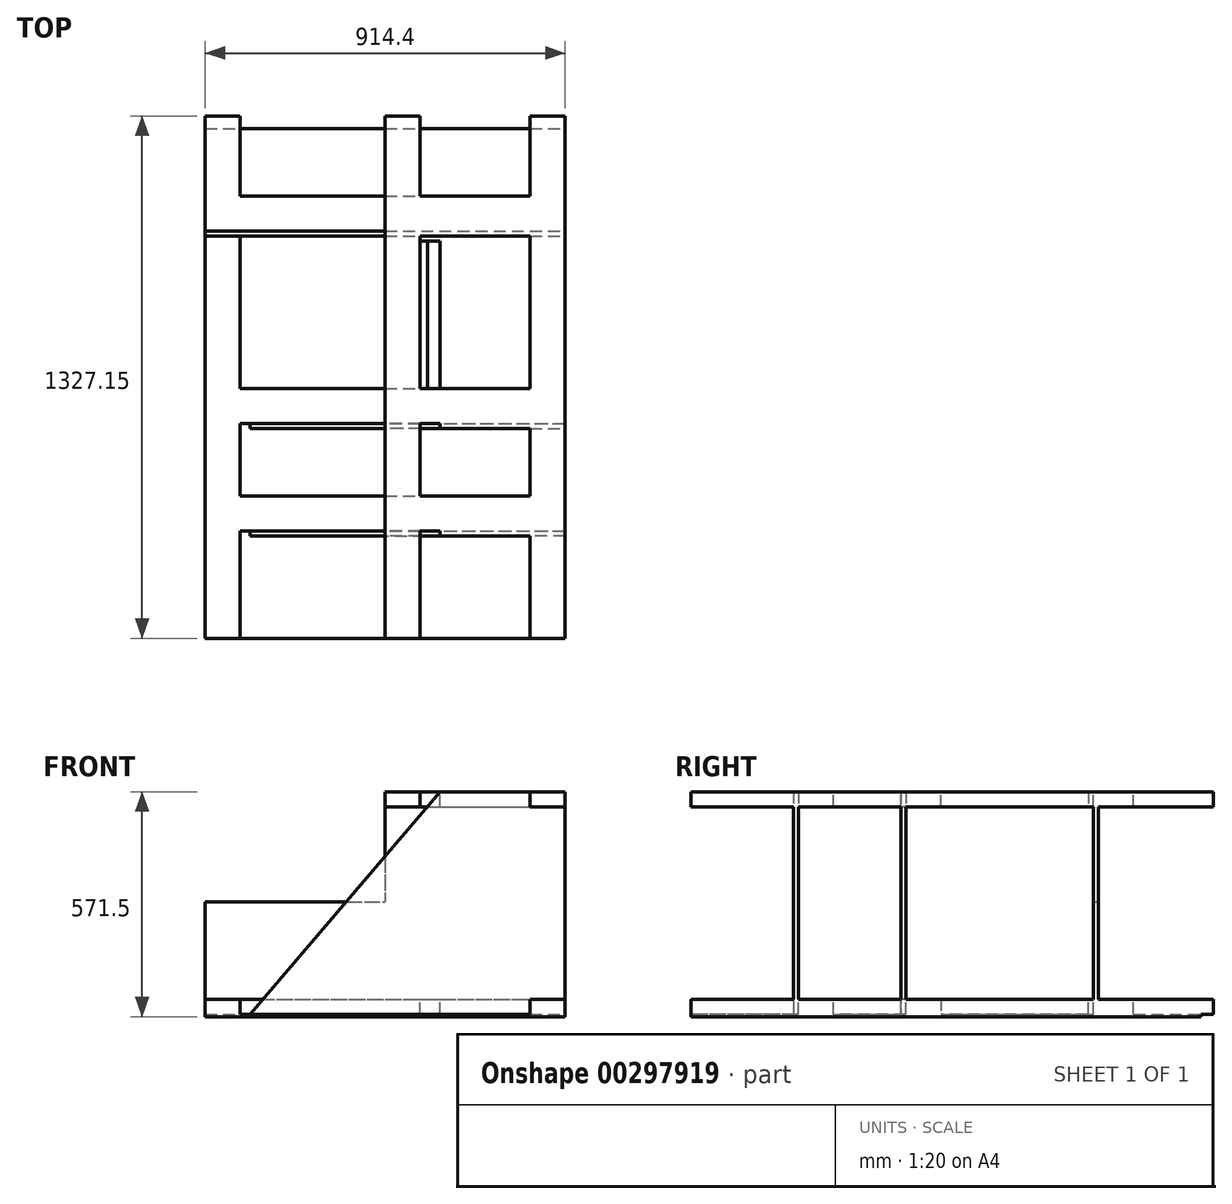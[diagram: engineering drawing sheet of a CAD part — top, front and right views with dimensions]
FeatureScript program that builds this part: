
annotation { "Feature Type Name" : "Feature", "Feature Type Description" : "" }
export const myFeature = defineFeature(function(context is Context, id is Id, definition is map)
    precondition{}
    {
        {
            var Q0;
            Q0=qCreatedBy(makeId("Front.planeOp"),FACE);
            var sketch = newSketch(context, id + "F0", { "sketchPlane" : qUnion([Q0])});
            skLineSegment(sketch, "E0.bottom", {"start": v(0, 0) * mm, "end": v(914.4, 0) * mm});
            skLineSegment(sketch, "E0.top", {"start": v(0, 565.15) * mm, "end": v(914.4, 565.15) * mm});
            skLineSegment(sketch, "E0.left", {"start": v(0, 0) * mm, "end": v(0, 565.15) * mm});
            skLineSegment(sketch, "E0.right", {"start": v(914.4, 0) * mm, "end": v(914.4, 565.15) * mm});
            skSolve(sketch);
        }
        {
            var Q0;
            Q0=makeQuery(id+"F0.imprint","IMPRINT",FACE,{"disambiguationData":[TD([[makeQuery(id+"F0.imprint","IMPRINT",EDGE,{"derivedFrom":sQuery(id+"F0.wireOp",EDGE,"E0.bottom")}),1.0]])]});
            extrude(context, id + "F1", {"entities" : qUnion([Q0]), "depth" : 1327.15 * mm});
        }
        {
            var Q0;
            Q0=makeQuery(id+"F1.opExtrude","SWEPT_FACE",FACE,{"disambiguationData":[OSD([sQuery(id+"F0.wireOp",EDGE,"E0.left")])]});
            var sketch = newSketch(context, id + "F2", { "sketchPlane" : qUnion([Q0])});
            skLineSegment(sketch, "E1.bottom", {"start": v(0, 565.15) * mm, "end": v(292.1, 565.15) * mm});
            skLineSegment(sketch, "E1.top", {"start": v(0, 285.75) * mm, "end": v(292.1, 285.75) * mm});
            skLineSegment(sketch, "E1.left", {"start": v(0, 565.15) * mm, "end": v(0, 285.75) * mm});
            skLineSegment(sketch, "E1.right", {"start": v(292.1, 565.15) * mm, "end": v(292.1, 285.75) * mm});
            skSolve(sketch);
        }
        {
            var Q0;
            Q0=makeQuery(id+"F2.imprint","IMPRINT",FACE,{"disambiguationData":[TD([[makeQuery(id+"F2.imprint","IMPRINT",EDGE,{"derivedFrom":sQuery(id+"F2.wireOp",EDGE,"E1.bottom")}),1.0]])]});
            extrude(context, id + "F3", {"entities" : qUnion([Q0]), "operationType" : NewBodyOperationType.REMOVE, "oppositeDirection" : true, "depth" : 457.2 * mm});
        }
        {
            var Q0;
            Q0=makeQuery(id+"F1.opExtrude","CAP_FACE",FACE,{"disambiguationData":[OSD([sQuery(id+"F0.wireOp",EDGE,"E0.bottom"),sQuery(id+"F0.wireOp",EDGE,"E0.top"),sQuery(id+"F0.wireOp",EDGE,"E0.left"),sQuery(id+"F0.wireOp",EDGE,"E0.right")])],"isStart":false});
            var sketch = newSketch(context, id + "F4", { "sketchPlane" : qUnion([Q0])});
            skLineSegment(sketch, "E2", {"start": v(825.5, 565.15) * mm, "end": v(825.5, 527.05) * mm});
            skLineSegment(sketch, "E3", {"start": v(825.5, 527.05) * mm, "end": v(914.4, 527.05) * mm});
            skLineSegment(sketch, "E4", {"start": v(825.5, 565.15) * mm, "end": v(546.1, 565.15) * mm});
            skLineSegment(sketch, "E5", {"start": v(914.4, 527.05) * mm, "end": v(914.4, 38.1) * mm});
            skLineSegment(sketch, "E6", {"start": v(914.4, 38.1) * mm, "end": v(825.5, 38.1) * mm});
            skLineSegment(sketch, "E7", {"start": v(825.5, 38.1) * mm, "end": v(825.5, 0) * mm});
            skLineSegment(sketch, "E8", {"start": v(825.5, 0) * mm, "end": v(88.9, 0) * mm});
            skLineSegment(sketch, "E9", {"start": v(88.9, 0) * mm, "end": v(88.9, 38.1) * mm});
            skLineSegment(sketch, "E10", {"start": v(88.9, 38.1) * mm, "end": v(0, 38.1) * mm});
            skLineSegment(sketch, "E11", {"start": v(0, 38.1) * mm, "end": v(0, 565.15) * mm});
            skLineSegment(sketch, "E12", {"start": v(546.1, 565.15) * mm, "end": v(546.1, 527.05) * mm});
            skLineSegment(sketch, "E13", {"start": v(546.1, 527.05) * mm, "end": v(457.2, 527.05) * mm});
            skLineSegment(sketch, "E14", {"start": v(457.2, 527.05) * mm, "end": v(457.2, 565.15) * mm});
            skLineSegment(sketch, "E15", {"start": v(457.2, 565.15) * mm, "end": v(0, 565.15) * mm});
            skSolve(sketch);
        }
        {
            var Q0;
            Q0=makeQuery(id+"F4.imprint","IMPRINT",FACE,{"disambiguationData":[TD([[makeQuery(id+"F4.imprint","IMPRINT",EDGE,{"derivedFrom":sQuery(id+"F4.wireOp",EDGE,"E2")}),-1.0]])]});
            extrude(context, id + "F5", {"entities" : qUnion([Q0]), "operationType" : NewBodyOperationType.REMOVE, "oppositeDirection" : true, "depth" : 260.35 * mm});
        }
        {
            var Q0;
            Q0=makeQuery(id+"F5.boolean.opBoolean","COPY",FACE,{"derivedFrom":makeQuery(id+"F5.opExtrude","CAP_FACE",FACE,{"disambiguationData":[OSD([sQuery(id+"F4.wireOp",EDGE,"E2"),sQuery(id+"F4.wireOp",EDGE,"E3"),sQuery(id+"F4.wireOp",EDGE,"E4"),sQuery(id+"F4.wireOp",EDGE,"E5"),sQuery(id+"F4.wireOp",EDGE,"E6"),sQuery(id+"F4.wireOp",EDGE,"E7"),sQuery(id+"F4.wireOp",EDGE,"E8"),sQuery(id+"F4.wireOp",EDGE,"E9"),sQuery(id+"F4.wireOp",EDGE,"E10"),sQuery(id+"F4.wireOp",EDGE,"E11"),sQuery(id+"F4.wireOp",EDGE,"E12"),sQuery(id+"F4.wireOp",EDGE,"E13"),sQuery(id+"F4.wireOp",EDGE,"E14"),sQuery(id+"F4.wireOp",EDGE,"E15")])],"isStart":false})});
            var sketch = newSketch(context, id + "F6", { "sketchPlane" : qUnion([Q0])});
            skLineSegment(sketch, "E16", {"start": v(596.9, 565.15) * mm, "end": v(825.5, 565.15) * mm});
            skLineSegment(sketch, "E17", {"start": v(825.5, 565.15) * mm, "end": v(825.5, 527.05) * mm});
            skLineSegment(sketch, "E18", {"start": v(825.5, 527.05) * mm, "end": v(914.4, 527.05) * mm});
            skLineSegment(sketch, "E19", {"start": v(914.4, 527.05) * mm, "end": v(914.4, 38.1) * mm});
            skLineSegment(sketch, "E20", {"start": v(914.4, 38.1) * mm, "end": v(825.5, 38.1) * mm});
            skLineSegment(sketch, "E21", {"start": v(825.5, 38.1) * mm, "end": v(825.5, 0) * mm});
            skLineSegment(sketch, "E22", {"start": v(596.9, 565.15) * mm, "end": v(114.3, 0) * mm});
            skLineSegment(sketch, "E23", {"start": v(114.3, 0) * mm, "end": v(825.5, 0) * mm});
            skSolve(sketch);
        }
        {
            var Q0;
            {var subQ2=sQuery(id+"F6.wireOp",EDGE,"E22");Q0=makeQuery(id+"F6.imprint","IMPRINT",FACE,{"disambiguationData":[TD([[makeQuery(id+"F6.imprint","IMPRINT",EDGE,{"derivedFrom":subQ2}),-1.0]])]});}
            extrude(context, id + "F7", {"entities" : qUnion([Q0]), "operationType" : NewBodyOperationType.REMOVE, "oppositeDirection" : true, "depth" : 749.3 * mm});
        }
        {
            var Q0;
            Q0=makeQuery(id+"F1.opExtrude","SWEPT_FACE",FACE,{"disambiguationData":[OSD([sQuery(id+"F0.wireOp",EDGE,"E0.right")])]});
            var sketch = newSketch(context, id + "F8", { "sketchPlane" : qUnion([Q0])});
            skLineSegment(sketch, "E24.bottom", {"start": v(-1054.1, 38.1) * mm, "end": v(-793.75, 38.1) * mm});
            skLineSegment(sketch, "E24.top", {"start": v(-1054.1, 527.05) * mm, "end": v(-793.75, 527.05) * mm});
            skLineSegment(sketch, "E24.left", {"start": v(-1054.1, 38.1) * mm, "end": v(-1054.1, 527.05) * mm});
            skLineSegment(sketch, "E24.right", {"start": v(-793.75, 38.1) * mm, "end": v(-793.75, 527.05) * mm});
            skLineSegment(sketch, "E25.bottom", {"start": v(-781.05, 38.1) * mm, "end": v(-304.8, 38.1) * mm});
            skLineSegment(sketch, "E25.top", {"start": v(-781.05, 527.05) * mm, "end": v(-304.8, 527.05) * mm});
            skLineSegment(sketch, "E25.left", {"start": v(-781.05, 38.1) * mm, "end": v(-781.05, 527.05) * mm});
            skLineSegment(sketch, "E25.right", {"start": v(-304.8, 38.1) * mm, "end": v(-304.8, 527.05) * mm});
            skLineSegment(sketch, "E26.bottom", {"start": v(-292.1, 38.1) * mm, "end": v(0, 38.1) * mm});
            skLineSegment(sketch, "E26.top", {"start": v(-292.1, 527.05) * mm, "end": v(0, 527.05) * mm});
            skLineSegment(sketch, "E26.left", {"start": v(-292.1, 38.1) * mm, "end": v(-292.1, 527.05) * mm});
            skLineSegment(sketch, "E26.right", {"start": v(0, 38.1) * mm, "end": v(0, 527.05) * mm});
            skSolve(sketch);
        }
        {
            var Q0;
            Q0=makeQuery(id+"F8.imprint","IMPRINT",FACE,{"disambiguationData":[TD([[makeQuery(id+"F8.imprint","IMPRINT",EDGE,{"derivedFrom":sQuery(id+"F8.wireOp",EDGE,"E24.bottom")}),1.0]])]});
            var Q1;
            Q1=makeQuery(id+"F8.imprint","IMPRINT",FACE,{"disambiguationData":[TD([[makeQuery(id+"F8.imprint","IMPRINT",EDGE,{"derivedFrom":sQuery(id+"F8.wireOp",EDGE,"E25.bottom")}),1.0]])]});
            var Q2;
            Q2=makeQuery(id+"F8.imprint","IMPRINT",FACE,{"disambiguationData":[TD([[makeQuery(id+"F8.imprint","IMPRINT",EDGE,{"derivedFrom":sQuery(id+"F8.wireOp",EDGE,"E26.bottom")}),1.0]])]});
            var Q3;
            Q3=makeQuery(id+"F1.opExtrude","SWEPT_FACE",FACE,{"disambiguationData":[OSD([sQuery(id+"F0.wireOp",EDGE,"E0.left")])]});
            extrude(context, id + "F9", {"entities" : qUnion([Q0, Q1, Q2]), "operationType" : NewBodyOperationType.REMOVE, "endBound" : BoundingType.UP_TO_SURFACE, "oppositeDirection" : true, "endBoundEntityFace" : qUnion([Q3]), "depth" : 25.4 * mm});
        }
        {
            var Q0;
            Q0=makeQuery(id+"F1.opExtrude","SWEPT_FACE",FACE,{"disambiguationData":[OSD([sQuery(id+"F0.wireOp",EDGE,"E0.top")])]});
            var sketch = newSketch(context, id + "F10", { "sketchPlane" : qUnion([Q0])});
            skLineSegment(sketch, "E27.bottom", {"start": v(825.5, -1054.1) * mm, "end": v(546.1, -1054.1) * mm});
            skLineSegment(sketch, "E27.top", {"start": v(825.5, -793.75) * mm, "end": v(546.1, -793.75) * mm});
            skLineSegment(sketch, "E27.left", {"start": v(825.5, -1054.1) * mm, "end": v(825.5, -793.75) * mm});
            skLineSegment(sketch, "E27.right", {"start": v(546.1, -1054.1) * mm, "end": v(546.1, -793.75) * mm});
            skLineSegment(sketch, "E28.bottom", {"start": v(825.5, -781.05) * mm, "end": v(546.1, -781.05) * mm});
            skLineSegment(sketch, "E28.top", {"start": v(825.5, -304.8) * mm, "end": v(546.1, -304.8) * mm});
            skLineSegment(sketch, "E28.left", {"start": v(825.5, -781.05) * mm, "end": v(825.5, -304.8) * mm});
            skLineSegment(sketch, "E28.right", {"start": v(546.1, -781.05) * mm, "end": v(546.1, -304.8) * mm});
            skLineSegment(sketch, "E29.bottom", {"start": v(825.5, 0) * mm, "end": v(546.1, 0) * mm});
            skLineSegment(sketch, "E29.top", {"start": v(825.5, -292.1) * mm, "end": v(546.1, -292.1) * mm});
            skLineSegment(sketch, "E29.left", {"start": v(825.5, 0) * mm, "end": v(825.5, -292.1) * mm});
            skLineSegment(sketch, "E29.right", {"start": v(546.1, 0) * mm, "end": v(546.1, -292.1) * mm});
            skSolve(sketch);
        }
        {
            var Q0;
            {var subQ0=sQuery(id+"F10.wireOp",EDGE,"E27.left");Q0=makeQuery(id+"F10.imprint","IMPRINT",FACE,{"disambiguationData":[TD([[makeQuery(id+"F10.imprint","IMPRINT",EDGE,{"derivedFrom":subQ0}),1.0]])]});}
            var Q1;
            {var subQ0=sQuery(id+"F10.wireOp",EDGE,"E28.left");Q1=makeQuery(id+"F10.imprint","IMPRINT",FACE,{"disambiguationData":[TD([[makeQuery(id+"F10.imprint","IMPRINT",EDGE,{"derivedFrom":subQ0}),1.0]])]});}
            var Q2;
            Q2=makeQuery(id+"F10.imprint","IMPRINT",FACE,{"disambiguationData":[TD([[makeQuery(id+"F10.imprint","IMPRINT",EDGE,{"derivedFrom":sQuery(id+"F10.wireOp",EDGE,"E29.bottom")}),-1.0]])]});
            var Q3;
            {var subQ0=sQuery(id+"F10.wireOp",EDGE,"E27.right");Q3=makeQuery(id+"F10.imprint","IMPRINT",FACE,{"disambiguationData":[TD([[makeQuery(id+"F10.imprint","IMPRINT",EDGE,{"derivedFrom":subQ0}),1.0]])]});}
            var Q4;
            {var subQ3=sQuery(id+"F4.wireOp",EDGE,"E4");var subQ7=makeQuery(id+"F7.boolean.opBoolean","COPY",EDGE,{"derivedFrom":makeQuery(id+"F7.opExtrude","CAP_EDGE",EDGE,{"disambiguationData":[OSD([subQ3])],"isStart":false})});Q4=makeQuery(id+"F10.imprint","IMPRINT",FACE,{"disambiguationData":[TD([[makeQuery(id+"F10.imprint","IMPRINT",EDGE,{"derivedFrom":subQ7}),-1.0]])]});}
            extrude(context, id + "F11", {"entities" : qUnion([Q0, Q1, Q2, Q3, Q4]), "operationType" : NewBodyOperationType.REMOVE, "endBound" : BoundingType.THROUGH_ALL, "oppositeDirection" : true, "depth" : 25.4 * mm});
        }
        {
            var Q0;
            Q0=makeQuery(id+"F1.opExtrude","SWEPT_FACE",FACE,{"disambiguationData":[OSD([sQuery(id+"F0.wireOp",EDGE,"E0.bottom")])]});
            var sketch = newSketch(context, id + "F12", { "sketchPlane" : qUnion([Q0])});
            skLineSegment(sketch, "E30.bottom", {"start": v(546.1, 1054.1) * mm, "end": v(114.3, 1054.1) * mm});
            skLineSegment(sketch, "E30.top", {"start": v(546.1, 793.75) * mm, "end": v(114.3, 793.75) * mm});
            skLineSegment(sketch, "E30.left", {"start": v(546.1, 1054.1) * mm, "end": v(546.1, 793.75) * mm});
            skLineSegment(sketch, "E30.right", {"start": v(114.3, 1054.1) * mm, "end": v(114.3, 793.75) * mm});
            skLineSegment(sketch, "E31.bottom", {"start": v(546.1, 781.05) * mm, "end": v(88.9, 781.05) * mm});
            skLineSegment(sketch, "E31.top", {"start": v(546.1, 304.8) * mm, "end": v(88.9, 304.8) * mm});
            skLineSegment(sketch, "E31.left", {"start": v(546.1, 781.05) * mm, "end": v(546.1, 304.8) * mm});
            skLineSegment(sketch, "E31.right", {"start": v(88.9, 781.05) * mm, "end": v(88.9, 304.8) * mm});
            skLineSegment(sketch, "E32.bottom", {"start": v(546.1, 292.1) * mm, "end": v(88.9, 292.1) * mm});
            skLineSegment(sketch, "E32.top", {"start": v(546.1, 0) * mm, "end": v(88.9, 0) * mm});
            skLineSegment(sketch, "E32.left", {"start": v(546.1, 292.1) * mm, "end": v(546.1, 0) * mm});
            skLineSegment(sketch, "E32.right", {"start": v(88.9, 292.1) * mm, "end": v(88.9, 0) * mm});
            skSolve(sketch);
        }
        {
            var Q0;
            Q0=makeQuery(id+"F12.imprint","IMPRINT",FACE,{"disambiguationData":[TD([[makeQuery(id+"F12.imprint","IMPRINT",EDGE,{"derivedFrom":sQuery(id+"F12.wireOp",EDGE,"E30.bottom")}),1.0]])]});
            var Q1;
            {var subQ1=sQuery(id+"F12.wireOp",EDGE,"E31.top");Q1=makeQuery(id+"F12.imprint","IMPRINT",FACE,{"disambiguationData":[TD([[makeQuery(id+"F12.imprint","IMPRINT",EDGE,{"derivedFrom":subQ1}),-1.0]])]});}
            var Q2;
            Q2=makeQuery(id+"F12.imprint","IMPRINT",FACE,{"disambiguationData":[TD([[makeQuery(id+"F12.imprint","IMPRINT",EDGE,{"derivedFrom":sQuery(id+"F12.wireOp",EDGE,"E32.bottom")}),1.0]])]});
            extrude(context, id + "F13", {"entities" : qUnion([Q0, Q1, Q2]), "operationType" : NewBodyOperationType.REMOVE, "oppositeDirection" : true, "depth" : 527.05 * mm});
        }
        {
            var Q0;
            Q0=makeQuery(id+"F13.boolean.opBoolean","MERGE",FACE,{"derivedFrom":[makeQuery(id+"F11.boolean.opBoolean","MERGE",FACE,{"derivedFrom":[makeQuery(id+"F9.boolean.opBoolean","MERGE",FACE,{"derivedFrom":[makeQuery(id+"F3.boolean.opBoolean","COPY",FACE,{"derivedFrom":makeQuery(id+"F3.opExtrude","SWEPT_FACE",FACE,{"disambiguationData":[OSD([sQuery(id+"F2.wireOp",EDGE,"E1.right")])]})}),makeQuery(id+"F9.opExtrude","SWEPT_FACE",FACE,{"disambiguationData":[OSD([sQuery(id+"F8.wireOp",EDGE,"E26.left")])]})]}),makeQuery(id+"F11.opExtrude","SWEPT_FACE",FACE,{"disambiguationData":[OSD([sQuery(id+"F10.wireOp",EDGE,"E29.top")])]})]}),makeQuery(id+"F13.opExtrude","SWEPT_FACE",FACE,{"disambiguationData":[OSD([sQuery(id+"F12.wireOp",EDGE,"E32.bottom")])]})]});
            var sketch = newSketch(context, id + "F14", { "sketchPlane" : qUnion([Q0])});
            skLineSegment(sketch, "E33.bottom", {"start": v(0, 565.15) * mm, "end": v(-457.2, 565.15) * mm});
            skLineSegment(sketch, "E33.top", {"start": v(0, 285.75) * mm, "end": v(-457.2, 285.75) * mm});
            skLineSegment(sketch, "E33.left", {"start": v(0, 565.15) * mm, "end": v(0, 285.75) * mm});
            skLineSegment(sketch, "E33.right", {"start": v(-457.2, 565.15) * mm, "end": v(-457.2, 285.75) * mm});
            skSolve(sketch);
        }
        {
            var Q0;
            {var subQ1=sQuery(id+"F14.wireOp",EDGE,"E33.bottom");Q0=makeQuery(id+"F14.imprint","IMPRINT",FACE,{"disambiguationData":[TD([[makeQuery(id+"F14.imprint","IMPRINT",EDGE,{"derivedFrom":subQ1}),-1.0]])]});}
            extrude(context, id + "F15", {"entities" : qUnion([Q0]), "operationType" : NewBodyOperationType.REMOVE, "oppositeDirection" : true, "depth" : 25.4 * mm});
        }
        {
            var Q0;
            Q0=makeQuery(id+"F1.opExtrude","SWEPT_FACE",FACE,{"disambiguationData":[OSD([sQuery(id+"F0.wireOp",EDGE,"E0.right")])]});
            var sketch = newSketch(context, id + "F16", { "sketchPlane" : qUnion([Q0])});
            skLineSegment(sketch, "E34.bottom", {"start": v(-1054.1, 527.05) * mm, "end": v(-965.2, 527.05) * mm});
            skLineSegment(sketch, "E34.top", {"start": v(-1054.1, 565.15) * mm, "end": v(-965.2, 565.15) * mm});
            skLineSegment(sketch, "E34.left", {"start": v(-1054.1, 527.05) * mm, "end": v(-1054.1, 565.15) * mm});
            skLineSegment(sketch, "E34.right", {"start": v(-965.2, 527.05) * mm, "end": v(-965.2, 565.15) * mm});
            skLineSegment(sketch, "E35.bottom", {"start": v(-781.05, 527.05) * mm, "end": v(-692.15, 527.05) * mm});
            skLineSegment(sketch, "E35.top", {"start": v(-781.05, 565.15) * mm, "end": v(-692.15, 565.15) * mm});
            skLineSegment(sketch, "E35.left", {"start": v(-781.05, 527.05) * mm, "end": v(-781.05, 565.15) * mm});
            skLineSegment(sketch, "E35.right", {"start": v(-692.15, 527.05) * mm, "end": v(-692.15, 565.15) * mm});
            skLineSegment(sketch, "E36.bottom", {"start": v(-292.1, 527.05) * mm, "end": v(-203.2, 527.05) * mm});
            skLineSegment(sketch, "E36.top", {"start": v(-292.1, 565.15) * mm, "end": v(-203.2, 565.15) * mm});
            skLineSegment(sketch, "E36.left", {"start": v(-292.1, 527.05) * mm, "end": v(-292.1, 565.15) * mm});
            skLineSegment(sketch, "E36.right", {"start": v(-203.2, 527.05) * mm, "end": v(-203.2, 565.15) * mm});
            skSolve(sketch);
        }
        {
            var Q0;
            Q0=makeQuery(id+"F16.imprint","IMPRINT",FACE,{"disambiguationData":[TD([[makeQuery(id+"F16.imprint","IMPRINT",EDGE,{"derivedFrom":sQuery(id+"F16.wireOp",EDGE,"E34.bottom")}),1.0]])]});
            var Q1;
            Q1=makeQuery(id+"F16.imprint","IMPRINT",FACE,{"disambiguationData":[TD([[makeQuery(id+"F16.imprint","IMPRINT",EDGE,{"derivedFrom":sQuery(id+"F16.wireOp",EDGE,"E35.bottom")}),1.0]])]});
            var Q2;
            Q2=makeQuery(id+"F16.imprint","IMPRINT",FACE,{"disambiguationData":[TD([[makeQuery(id+"F16.imprint","IMPRINT",EDGE,{"derivedFrom":sQuery(id+"F16.wireOp",EDGE,"E36.bottom")}),1.0]])]});
            var Q3;
            {var subQ0=sQuery(id+"F4.wireOp",EDGE,"E12");Q3=makeQuery(id+"F11.boolean.opBoolean","MERGE",FACE,{"derivedFrom":[makeQuery(id+"F7.boolean.opBoolean","MERGE",FACE,{"derivedFrom":[makeQuery(id+"F5.boolean.opBoolean","COPY",FACE,{"derivedFrom":makeQuery(id+"F5.opExtrude","SWEPT_FACE",FACE,{"disambiguationData":[OSD([subQ0])]})}),makeQuery(id+"F7.opExtrude","SWEPT_FACE",FACE,{"disambiguationData":[OSD([subQ0])]})]}),makeQuery(id+"F11.opExtrude","SWEPT_FACE",FACE,{"disambiguationData":[OSD([sQuery(id+"F10.wireOp",EDGE,"E28.right")])]})]});}
            extrude(context, id + "F17", {"entities" : qUnion([Q0, Q1, Q2]), "operationType" : NewBodyOperationType.ADD, "endBound" : BoundingType.UP_TO_SURFACE, "oppositeDirection" : true, "endBoundEntityFace" : qUnion([Q3]), "depth" : 25.4 * mm});
        }
        {
            var Q0;
            Q0=makeQuery(id+"F1.opExtrude","SWEPT_FACE",FACE,{"disambiguationData":[OSD([sQuery(id+"F0.wireOp",EDGE,"E0.right")])]});
            var sketch = newSketch(context, id + "F18", { "sketchPlane" : qUnion([Q0])});
            skLineSegment(sketch, "E37.bottom", {"start": v(-1054.1, 38.1) * mm, "end": v(-965.2, 38.1) * mm});
            skLineSegment(sketch, "E37.top", {"start": v(-1054.1, 0) * mm, "end": v(-965.2, 0) * mm});
            skLineSegment(sketch, "E37.left", {"start": v(-1054.1, 38.1) * mm, "end": v(-1054.1, 0) * mm});
            skLineSegment(sketch, "E37.right", {"start": v(-965.2, 38.1) * mm, "end": v(-965.2, 0) * mm});
            skLineSegment(sketch, "E38.bottom", {"start": v(-781.05, 38.1) * mm, "end": v(-692.15, 38.1) * mm});
            skLineSegment(sketch, "E38.top", {"start": v(-781.05, 0) * mm, "end": v(-692.15, 0) * mm});
            skLineSegment(sketch, "E38.left", {"start": v(-781.05, 38.1) * mm, "end": v(-781.05, 0) * mm});
            skLineSegment(sketch, "E38.right", {"start": v(-692.15, 38.1) * mm, "end": v(-692.15, 0) * mm});
            skLineSegment(sketch, "E39.bottom", {"start": v(-292.1, 38.1) * mm, "end": v(-203.2, 38.1) * mm});
            skLineSegment(sketch, "E39.top", {"start": v(-292.1, 0) * mm, "end": v(-203.2, 0) * mm});
            skLineSegment(sketch, "E39.left", {"start": v(-292.1, 38.1) * mm, "end": v(-292.1, 0) * mm});
            skLineSegment(sketch, "E39.right", {"start": v(-203.2, 38.1) * mm, "end": v(-203.2, 0) * mm});
            skSolve(sketch);
        }
        {
            var Q0;
            Q0=makeQuery(id+"F18.imprint","IMPRINT",FACE,{"disambiguationData":[TD([[makeQuery(id+"F18.imprint","IMPRINT",EDGE,{"derivedFrom":sQuery(id+"F18.wireOp",EDGE,"E37.bottom")}),-1.0]])]});
            var Q1;
            Q1=makeQuery(id+"F18.imprint","IMPRINT",FACE,{"disambiguationData":[TD([[makeQuery(id+"F18.imprint","IMPRINT",EDGE,{"derivedFrom":sQuery(id+"F18.wireOp",EDGE,"E38.bottom")}),-1.0]])]});
            var Q2;
            Q2=makeQuery(id+"F18.imprint","IMPRINT",FACE,{"disambiguationData":[TD([[makeQuery(id+"F18.imprint","IMPRINT",EDGE,{"derivedFrom":sQuery(id+"F18.wireOp",EDGE,"E39.bottom")}),-1.0]])]});
            var Q3;
            {var subQ0=sQuery(id+"F4.wireOp",EDGE,"E9");Q3=makeQuery(id+"F13.boolean.opBoolean","MERGE",FACE,{"derivedFrom":[makeQuery(id+"F7.boolean.opBoolean","MERGE",FACE,{"derivedFrom":[makeQuery(id+"F5.boolean.opBoolean","COPY",FACE,{"derivedFrom":makeQuery(id+"F5.opExtrude","SWEPT_FACE",FACE,{"disambiguationData":[OSD([subQ0])]})}),makeQuery(id+"F7.opExtrude","SWEPT_FACE",FACE,{"disambiguationData":[OSD([subQ0])]})]}),makeQuery(id+"F13.opExtrude","SWEPT_FACE",FACE,{"disambiguationData":[OSD([sQuery(id+"F12.wireOp",EDGE,"E31.right")])]})]});}
            extrude(context, id + "F19", {"entities" : qUnion([Q0, Q1, Q2]), "operationType" : NewBodyOperationType.ADD, "endBound" : BoundingType.UP_TO_SURFACE, "oppositeDirection" : true, "endBoundEntityFace" : qUnion([Q3]), "depth" : 25.4 * mm});
        }
        {
            var Q0;
            Q0=makeQuery(id+"F19.boolean.opBoolean","MERGE",FACE,{"derivedFrom":[makeQuery(id+"F1.opExtrude","SWEPT_FACE",FACE,{"disambiguationData":[OSD([sQuery(id+"F0.wireOp",EDGE,"E0.bottom")])]}),makeQuery(id+"F19.opExtrude","SWEPT_FACE",FACE,{"disambiguationData":[OSD([sQuery(id+"F18.wireOp",EDGE,"E37.top")])]}),makeQuery(id+"F19.opExtrude","SWEPT_FACE",FACE,{"disambiguationData":[OSD([sQuery(id+"F18.wireOp",EDGE,"E38.top")])]}),makeQuery(id+"F19.opExtrude","SWEPT_FACE",FACE,{"disambiguationData":[OSD([sQuery(id+"F18.wireOp",EDGE,"E39.top")])]})]});
            var sketch = newSketch(context, id + "F20", { "sketchPlane" : qUnion([Q0])});
            skLineSegment(sketch, "E40.bottom", {"start": v(0, 1327.15) * mm, "end": v(914.4, 1327.15) * mm});
            skLineSegment(sketch, "E40.top", {"start": v(0, 31.75) * mm, "end": v(914.4, 31.75) * mm});
            skLineSegment(sketch, "E40.left", {"start": v(0, 1327.15) * mm, "end": v(0, 31.75) * mm});
            skLineSegment(sketch, "E40.right", {"start": v(914.4, 1327.15) * mm, "end": v(914.4, 31.75) * mm});
            skSolve(sketch);
        }
        {
            var Q0;
            Q0 = qSketchRegion(id + "F20", true);
            extrude(context, id + "F21", {"entities" : qUnion([Q0]), "operationType" : NewBodyOperationType.ADD, "depth" : 6.35 * mm});
        }
    });
